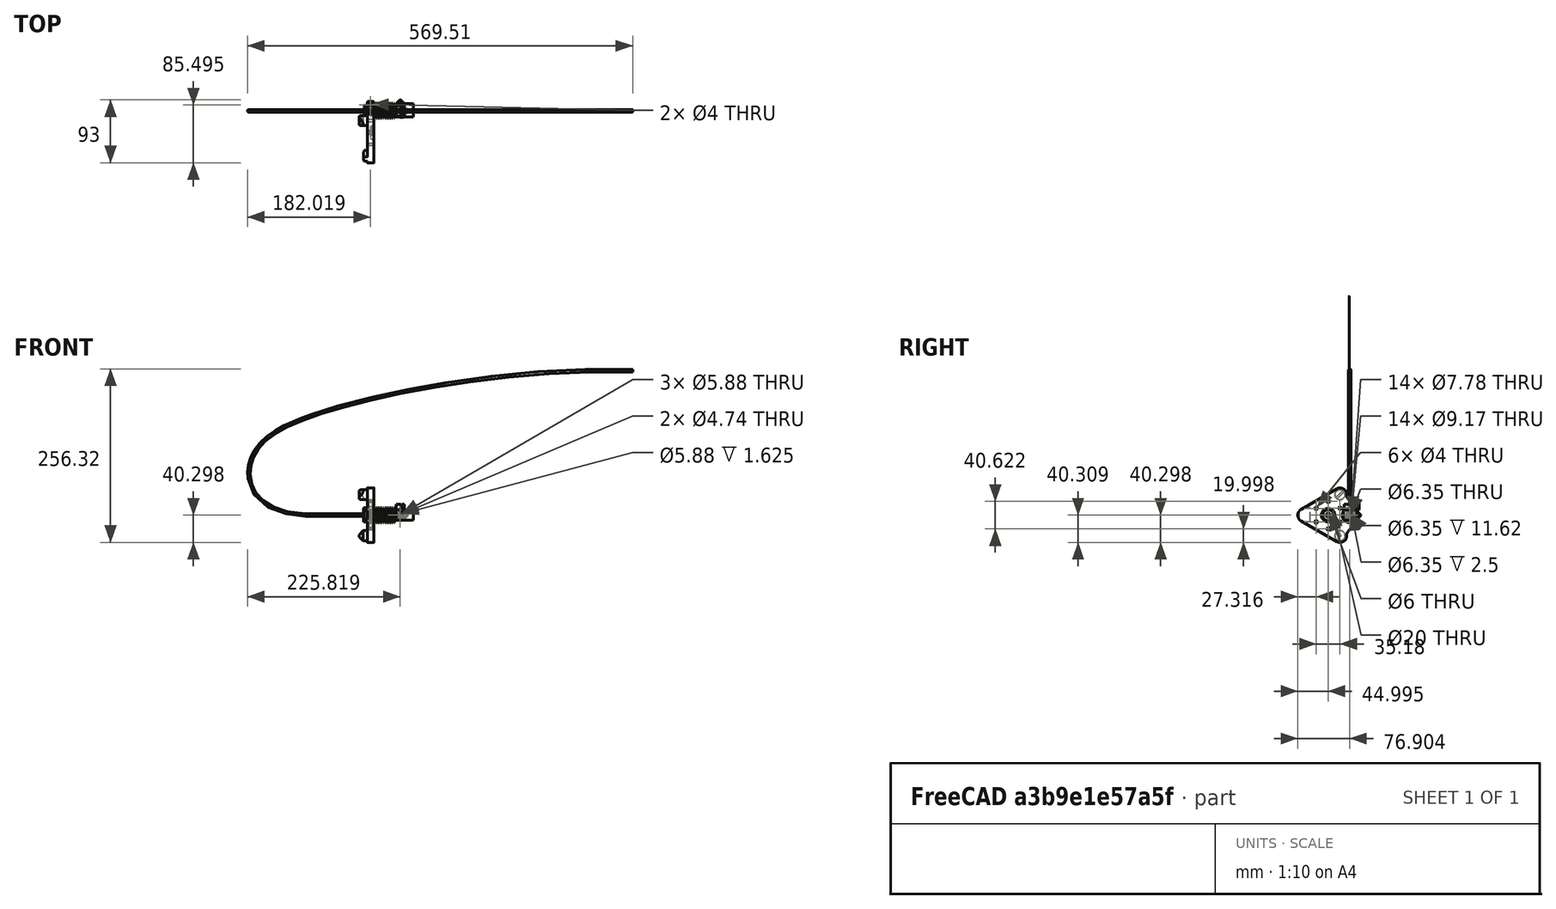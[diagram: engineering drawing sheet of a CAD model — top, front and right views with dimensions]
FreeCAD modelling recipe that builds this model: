
FCSTD DOCUMENT  (FreeCAD 0.20R29177 (Git))
Label: AT_931a_hotend
License: All rights reserved
LicenseURL: http://en.wikipedia.org/wiki/All_rights_reserved
objects: Part::FeaturePython×2, App::FeaturePython×2, PartDesign::ShapeBinder×2, Sketcher::SketchObject×2, PartDesign::AdditivePipe×1, PartDesign::Body×1
note: 9 computed .brp shape members not serialized (recipe doc carries the construction recipe); baked Part::Feature solids carry a one-line shape summary decoded from their .brp

FEATURE [Part::FeaturePython] b_AP_012a_toolHolder_GA3Dtech_001_  label="AP_012a_toolHolder_GA3Dtech_001"  # a2plus imported part (geometry in sourceFile) (typed FeaturePython)
  a2p_Version = V0.1
  fixedPosition = true
  objectType = a2pPart
  sourceFile = ./AP_012a_toolHolder_GA3Dtech.FCStd
  subassemblyImport = false
  timeLastImport = 1656487314
  updateColors = true
FEATURE [Part::FeaturePython] b_AT_hotend_horizontal_001_  label="AT_hotend_horizontal_001"  # a2plus imported part (geometry in sourceFile) (typed FeaturePython)
  Placement = pos=(-4.94089,57.1337,6.03789) rot=(0,1,0;4.71239rad)
  a2p_Version = V0.1
  fixedPosition = false
  objectType = a2pPart
  sourceFile = ./AT_hotend_horizontal.FCStd
  subassemblyImport = false
  timeLastImport = 1656523934
  updateColors = true
FEATURE [App::FeaturePython] planeCoincident_001  label="planeCoincident_001__AP_012a_toolHolder_GA3Dtech_001"  # a2plus constraint (typed FeaturePython)
  Object1 = b_AT_hotend_horizontal_001_
  Object2 = b_AP_012a_toolHolder_GA3Dtech_001_
  ParentTreeObject = -> b_AT_hotend_horizontal_001_
  SubElement1 = Face92
  SubElement2 = Face3
  Suppressed = false
  Type = plane
  directionConstraint = 0
  offset = 0
FEATURE [App::FeaturePython] planeCoincident_001_mirror  label="planeCoincident_001__AT_hotend_horizontal_001"  # a2plus constraint (typed FeaturePython)
  Object1 = b_AT_hotend_horizontal_001_
  Object2 = b_AP_012a_toolHolder_GA3Dtech_001_
  ParentTreeObject = -> b_AP_012a_toolHolder_GA3Dtech_001_
  SubElement1 = Face92
  SubElement2 = Face3
  Suppressed = false
  Type = plane
  directionConstraint = 0
  offset = 0
FEATURE [PartDesign::ShapeBinder] ShapeBinder
  Placement = pos=(-4.94089,57.1337,6.03789) rot=(0,-1,0;1.5708rad)
  Support = -> [b_AT_hotend_horizontal_001_]
  TraceSupport = false
FEATURE [Sketcher::SketchObject] Sketch001
  FullyConstrained = false
  MapMode = 5
  Placement = pos=(-4.94089,57.1337,6.03789) rot=(0,-1,0;1.5708rad)
  Support = -> [ShapeBinder]
  sketch-geometry (2):
    g0: Circle CenterX=0 CenterY=-1e-06 CenterZ=0 NormalX=0 NormalY=0 NormalZ=1 AngleXU=0 Radius=2
    g1: Circle CenterX=0 CenterY=-1e-06 CenterZ=0 NormalX=0 NormalY=0 NormalZ=1 AngleXU=0 Radius=0.861519
  constraints (2):
    c: Diameter(g0) = 4
    c: Coincident(g1,g0)
FEATURE [PartDesign::ShapeBinder] ShapeBinder001
  Support = -> [b_AP_012a_toolHolder_GA3Dtech_001_]
  TraceSupport = false
FEATURE [Sketcher::SketchObject] Sketch
  FullyConstrained = false
  MapMode = 5
  Placement = pos=(0,70.725,0) rot=(0,0.707107,0.707107;3.14159rad)
  Support = -> [ShapeBinder001]
  sketch-geometry (12):
    g0: LineSegment StartX=4.79604 StartY=5.93311 StartZ=0 EndX=92.6904 EndY=5.93311 EndZ=0
    g1-g6: Circle x6 (B-spline internal-alignment scaffolding for g7; pole/knot coordinates omitted)
    g7: BSplineCurve PolesCount=6 KnotsCount=4 Degree=3 IsPeriodic=0
    g8-g11: GeomPoint x4 (B-spline internal-alignment scaffolding for g7; pole/knot coordinates omitted)
  constraints (6):
    c: Horizontal(g0)
    c: Weight(g1) = 1
    c: Coincident(g7,g0)
    c: Equal(g1, g2-g6) x5
    c: InternalAlignment(g1-g6 -> g7) x6
    c: InternalAlignment(g8-g11 -> g7) x4
FEATURE [PartDesign::AdditivePipe] AdditivePipe
  AuxilleryCurvelinear = true
  AuxillerySpineTangent = false
  Binormal = (0,0,0)
  Mode = 0
  Placement = pos=(-4.94089,57.1337,6.03789) rot=(0,-1,0;1.5708rad)
  Profile = -> Sketch001
  Spine = -> Sketch
  SpineTangent = false
  Transformation = 0
  Transition = 0
FEATURE [PartDesign::Body] Body
  Group = -> [ShapeBinder,Sketch001,ShapeBinder001,Sketch,AdditivePipe]
  Origin = -> Origin
  Tip = -> AdditivePipe
